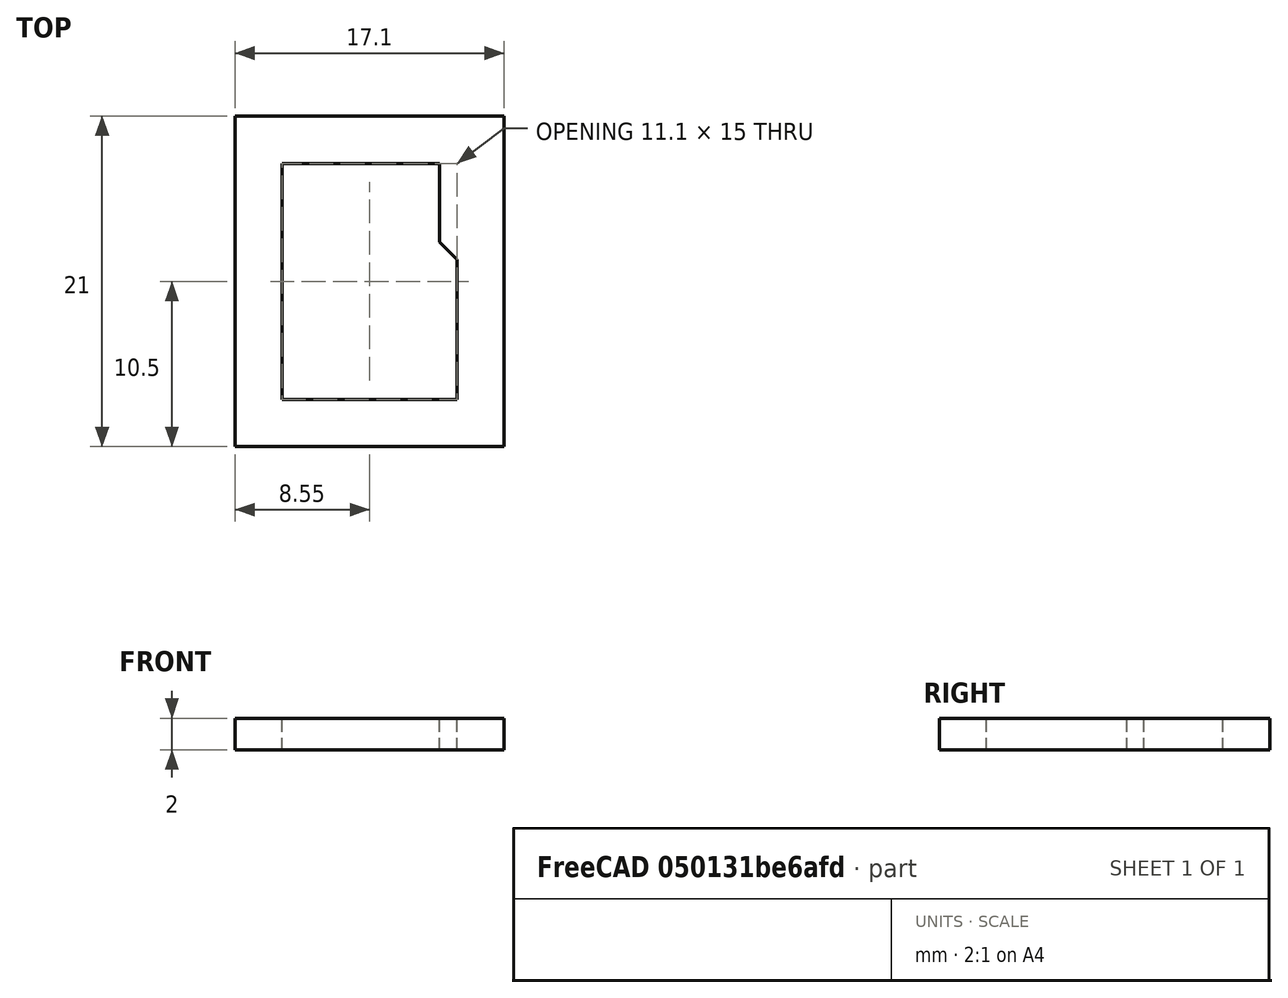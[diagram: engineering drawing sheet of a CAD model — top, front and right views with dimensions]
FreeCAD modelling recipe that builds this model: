
FCSTD DOCUMENT  (FreeCAD 0.19R24267 +99 (Git))
Label: SD-Slot
License: All rights reserved
LicenseURL: http://en.wikipedia.org/wiki/All_rights_reserved
objects: Sketcher::SketchObject×1, PartDesign::Pad×1, PartDesign::Body×1
note: 4 computed .brp shape members not serialized (recipe doc carries the construction recipe); baked Part::Feature solids carry a one-line shape summary decoded from their .brp

FEATURE [Sketcher::SketchObject] Sketch
  FullyConstrained = true
  MapMode = 5
  Support = -> [XY_Plane001]
  sketch-geometry (10):
    g0: LineSegment StartX=0 StartY=15 StartZ=0 EndX=10 EndY=15 EndZ=0
    g1: LineSegment StartX=11.1 StartY=0 StartZ=0 EndX=0 EndY=0 EndZ=0
    g2: LineSegment StartX=0 StartY=0 StartZ=0 EndX=0 EndY=15 EndZ=0
    g3: LineSegment StartX=10 StartY=15 StartZ=0 EndX=10 EndY=10 EndZ=0
    g4: LineSegment StartX=10 StartY=10 StartZ=0 EndX=11.1 EndY=8.9 EndZ=0
    g5: LineSegment StartX=11.1 StartY=8.9 StartZ=0 EndX=11.1 EndY=0 EndZ=0
    g6: LineSegment StartX=-3 StartY=18 StartZ=0 EndX=14.1 EndY=18 EndZ=0
    g7: LineSegment StartX=14.1 StartY=18 StartZ=0 EndX=14.1 EndY=-3 EndZ=0
    g8: LineSegment StartX=14.1 StartY=-3 StartZ=0 EndX=-3 EndY=-3 EndZ=0
    g9: LineSegment StartX=-3 StartY=-3 StartZ=0 EndX=-3 EndY=18 EndZ=0
  constraints (29):
    c: Horizontal(g0)
    c: Horizontal(g1)
    c: Coincident(g1,g2)
    c: Coincident(g2,g0)
    c: Vertical(g2)
    c: Distance(g2) = 15
    c: Distance(g1) = 11.1
    c: Coincident(g-1,g1)
    c: Distance(g0) = 10
    c: Coincident(g0,g3)
    c: Vertical(g3)
    c: Coincident(g3,g4)
    c: Coincident(g4,g5)
    c: Vertical(g5)
    c: Distance(g3) = 5
    c: Angle(g4,g3) = 2.35619
    c: Coincident(g1,g5)
    c: Coincident(g6,g7)
    c: Coincident(g7,g8)
    c: Coincident(g8,g9)
    c: Coincident(g9,g6)
    c: Horizontal(g6)
    c: Horizontal(g8)
    c: Vertical(g7)
    c: Vertical(g9)
    c: Distance(g0,g6) = 3
    c: Distance(g0,g9) = 3
    c: Distance(g1,g7) = 3
    c: Distance(g1,g8) = 3
FEATURE [PartDesign::Pad] Pad
  Direction = (1,1,1)
  Length = 2
  Length2 = 100
  Profile = -> Sketch
  Type = 0
FEATURE [PartDesign::Body] Body
  Group = -> [Sketch,Pad]
  Origin = -> Origin001
  Tip = -> Pad
